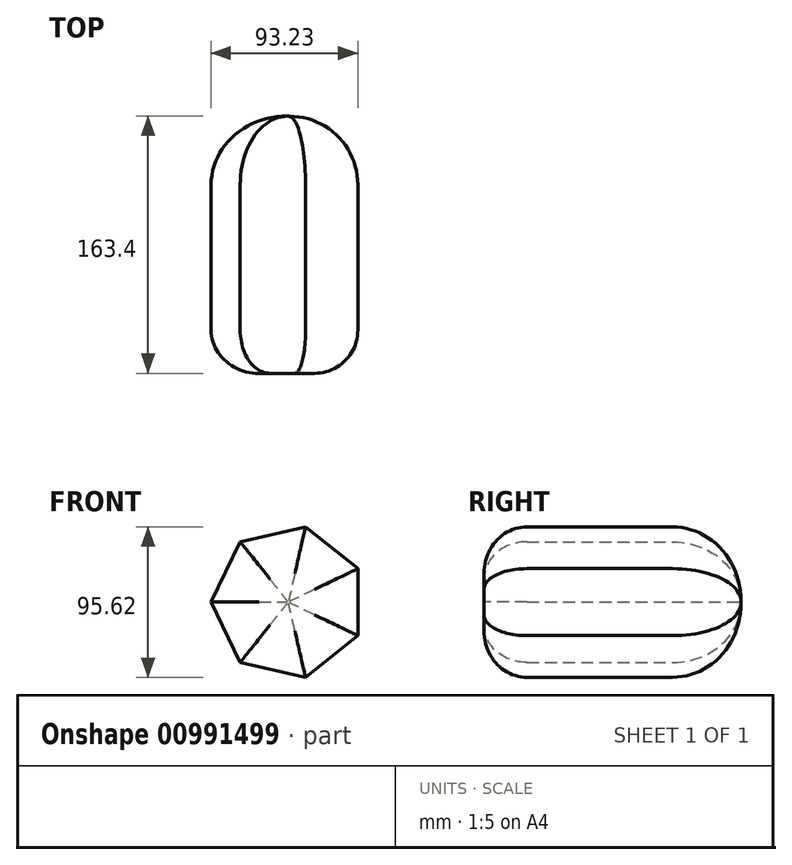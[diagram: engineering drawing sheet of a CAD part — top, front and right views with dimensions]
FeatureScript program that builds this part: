
annotation { "Feature Type Name" : "Feature", "Feature Type Description" : "" }
export const myFeature = defineFeature(function(context is Context, id is Id, definition is map)
    precondition{}
    {
        {
            var Q0;
            Q0=qCreatedBy(makeId("Front.planeOp"),FACE);
            var sketch = newSketch(context, id + "F0", { "sketchPlane" : qUnion([Q0])});
            skCircle(sketch, "E0.cCircle", {"center": v(-20.75, 0) * mm, "radius": 44.19 * mm, "construction": true});
            skLineSegment(sketch, "E0.0", {"start": v(23.43, 21.28) * mm, "end": v(23.43, -21.28) * mm});
            skLineSegment(sketch, "E0.1", {"start": v(23.43, -21.28) * mm, "end": v(-9.84, -47.81) * mm});
            skLineSegment(sketch, "E0.2", {"start": v(-9.84, -47.81) * mm, "end": v(-51.33, -38.34) * mm});
            skLineSegment(sketch, "E0.3", {"start": v(-51.33, -38.34) * mm, "end": v(-69.8, 0) * mm});
            skLineSegment(sketch, "E0.4", {"start": v(-69.8, 0) * mm, "end": v(-51.33, 38.34) * mm});
            skLineSegment(sketch, "E0.5", {"start": v(-51.33, 38.34) * mm, "end": v(-9.84, 47.81) * mm});
            skLineSegment(sketch, "E0.6", {"start": v(-9.84, 47.81) * mm, "end": v(23.43, 21.28) * mm});
            skPoint(sketch, "E0.0.midPoint", {"position": v(23.43, 0) * mm});
            skSolve(sketch);
        }
        {
            var Q0;
            Q0=makeQuery(id+"F0.imprint","IMPRINT",FACE,{"disambiguationData":[TD([[makeQuery(id+"F0.imprint","IMPRINT",EDGE,{"derivedFrom":sQuery(id+"F0.wireOp",EDGE,"E0.0")}),-1.0]])]});
            extrude(context, id + "F1", {"entities" : qUnion([Q0]), "depth" : 163.4 * mm, "offsetDistance" : 25.4 * mm});
        }
        {
            var Q0;
            Q0=makeQuery(id+"F1.opExtrude","CAP_EDGE",EDGE,{"disambiguationData":[OSD([sQuery(id+"F0.wireOp",EDGE,"E0.5")])],"isStart":false});
            var Q1;
            Q1=makeQuery(id+"F1.opExtrude","CAP_EDGE",EDGE,{"disambiguationData":[OSD([sQuery(id+"F0.wireOp",EDGE,"E0.4")])],"isStart":false});
            var Q2;
            Q2=makeQuery(id+"F1.opExtrude","CAP_EDGE",EDGE,{"disambiguationData":[OSD([sQuery(id+"F0.wireOp",EDGE,"E0.3")])],"isStart":false});
            var Q3;
            Q3=makeQuery(id+"F1.opExtrude","CAP_EDGE",EDGE,{"disambiguationData":[OSD([sQuery(id+"F0.wireOp",EDGE,"E0.2")])],"isStart":false});
            var Q4;
            Q4=makeQuery(id+"F1.opExtrude","CAP_EDGE",EDGE,{"disambiguationData":[OSD([sQuery(id+"F0.wireOp",EDGE,"E0.6")])],"isStart":false});
            var Q5;
            Q5=makeQuery(id+"F1.opExtrude","CAP_EDGE",EDGE,{"disambiguationData":[OSD([sQuery(id+"F0.wireOp",EDGE,"E0.0")])],"isStart":false});
            var Q6;
            Q6=makeQuery(id+"F1.opExtrude","CAP_EDGE",EDGE,{"disambiguationData":[OSD([sQuery(id+"F0.wireOp",EDGE,"E0.1")])],"isStart":false});
            fillet(context, id + "F2", {"entities" : qUnion([Q0, Q1, Q2, Q3, Q4, Q5, Q6]), "radius" : 27.4 * mm, "tangentPropagation" : true, "allowEdgeOverflow" : false});
        }
        {
            var Q0;
            Q0=makeQuery(id+"F1.opExtrude","CAP_EDGE",EDGE,{"disambiguationData":[OSD([sQuery(id+"F0.wireOp",EDGE,"E0.5")])],"isStart":true});
            var Q1;
            Q1=makeQuery(id+"F1.opExtrude","CAP_EDGE",EDGE,{"disambiguationData":[OSD([sQuery(id+"F0.wireOp",EDGE,"E0.6")])],"isStart":true});
            var Q2;
            Q2=makeQuery(id+"F1.opExtrude","CAP_EDGE",EDGE,{"disambiguationData":[OSD([sQuery(id+"F0.wireOp",EDGE,"E0.0")])],"isStart":true});
            var Q3;
            Q3=makeQuery(id+"F1.opExtrude","CAP_EDGE",EDGE,{"disambiguationData":[OSD([sQuery(id+"F0.wireOp",EDGE,"E0.1")])],"isStart":true});
            var Q4;
            Q4=makeQuery(id+"F1.opExtrude","CAP_EDGE",EDGE,{"disambiguationData":[OSD([sQuery(id+"F0.wireOp",EDGE,"E0.2")])],"isStart":true});
            var Q5;
            Q5=makeQuery(id+"F1.opExtrude","CAP_EDGE",EDGE,{"disambiguationData":[OSD([sQuery(id+"F0.wireOp",EDGE,"E0.4")])],"isStart":true});
            var Q6;
            Q6=makeQuery(id+"F1.opExtrude","CAP_EDGE",EDGE,{"disambiguationData":[OSD([sQuery(id+"F0.wireOp",EDGE,"E0.3")])],"isStart":true});
            var Q7;
            Q7=makeQuery(id+"F1.opExtrude","CAP_FACE",FACE,{"disambiguationData":[OSD([sQuery(id+"F0.wireOp",EDGE,"E0.0"),sQuery(id+"F0.wireOp",EDGE,"E0.1"),sQuery(id+"F0.wireOp",EDGE,"E0.2"),sQuery(id+"F0.wireOp",EDGE,"E0.3"),sQuery(id+"F0.wireOp",EDGE,"E0.4"),sQuery(id+"F0.wireOp",EDGE,"E0.5"),sQuery(id+"F0.wireOp",EDGE,"E0.6")])],"isStart":true});
            fillet(context, id + "F3", {"entities" : qUnion([Q0, Q1, Q2, Q3, Q4, Q5, Q6, Q7]), "radius" : 43.53 * mm, "tangentPropagation" : true, "allowEdgeOverflow" : false});
        }
    });
